# Revit family: Rohrschelle Maxima PSM, M 8-M10, Ø 15- 64, Gummi
name_source: partatom
category: HLS-Bauteile
revit_build: Autodesk Revit 2017 (Build: 20190507_1515(x64)
units: mm (PartAtom-declared; Revit-internal decimal feet)

## family parameters
Arbeitsebenenbasiert = Nein
Beim Laden mit Abzugskörper schneiden = Nein
Bemaßung runder Anschluss = Durchmesser verwenden
Gemeinsam genutzt = Ja
Immer vertikal = Nein
Raumberechnungspunkt = Nein
Teiletyp = Normal

## types (8) — shared parameters
A = 31 mm  [stored 0.101706 ft]
Anschluss = M8/M10
Anschlußhöhe = 30 mm
Bauart = zweiteilig
Baustoffklasse = B2
Brandschutz = RAL-GZ 656
DF1 = 24 mm  [stored 0.0787402 ft]
DF2 = 20 mm  [stored 0.0656168 ft]
DS = 6 mm  [stored 0.019685 ft]
DVS = 15 mm  [stored 0.0492126 ft]
Dämmstärke = 6 mm  [stored 0.019685 ft]
Fabrikat = MEFA
Farbe Schalldämmeinlage = schwarz
Firma = MEFA Befestigungs- und Montagesysteme GmbH
HGA = 22 mm  [stored 0.0721785 ft]
Kurztext1 = Rohrschelle Maxima PSM 25x3,0
MB = 25 mm  [stored 0.082021 ft]
MD = 3 mm  [stored 0.00984252 ft]
Material = Stahl
Material Schalldämmeinlage = TPE
Materialmaße = 25x3,0 mm
Materialname = S235
Mengeneinheit = St
Oberflaeche = galvanisch verzinkt
Schalldämmeinlage = Gummi
Verschluss = Pendelsteckmuttern
Verschluss-Schraube = M8
max. Temperaturbeständigkeit = 100 °C
max. zul. Last = 1.50 kN
max. zul. Last horizontal = 0.00 kN
max. zul. Last vertikal = 0.00 kN
vpe = 1 St
zero-valued in all types: Nennweite DN Rohr, Rohraußendurchmesser, Stärke Material

## per-type parameters (varying)
| type | AB | Achsabstand | Artikelnummer | B | Breite | D | D0 | Dmax | Dmin | EAN | Gewicht | Gewicht pro Bauteil | H | Kurztext2 | R | RM | Rohraußendurchmesser Zoll | S | max. Höhe | max. Rohraußendurchmesser | min. Rohraußendurchmesser |
| Maxima PSM, M8/M10, Ø 15- 19, Gummi | 4 mm  [stored 0.0131234 ft] | 57 mm | 0068819 | 81 mm | 81 mm | 19 mm  [stored 0.062336 ft] | 31 mm  [stored 0.101706 ft] | 19 mm  [stored 0.062336 ft] | 15 mm  [stored 0.0492126 ft] | 4250928402363 | 0.20 kg | 0.20 kg | 59 mm  [stored 0.19357 ft] | 15 - 19 mm M8/M10 TPE | 16 mm  [stored 0.0524934 ft] | 19 mm  [stored 0.062336 ft] | Zoll | 57 mm  [stored 0.187008 ft] | 58 mm  [stored 0.190289 ft] | 19 mm  [stored 0.062336 ft] | 15 mm  [stored 0.0492126 ft] |
| Maxima PSM, M8/M10, Ø 20- 25, Gummi | 5 mm  [stored 0.0164042 ft] | 63 mm | 0068823 | 87 mm | 87 mm | 25 mm  [stored 0.082021 ft] | 37 mm  [stored 0.121391 ft] | 25 mm  [stored 0.082021 ft] | 20 mm  [stored 0.0656168 ft] | 4250928402370 | 0.21 kg | 0.21 kg | 65 mm  [stored 0.213255 ft] | 20 - 25 mm M8/M10 TPE | 19 mm  [stored 0.062336 ft] | 22 mm  [stored 0.0721785 ft] | 1/2 Zoll | 63 mm | 64 mm  [stored 0.209974 ft] | 25 mm  [stored 0.082021 ft] | 20 mm  [stored 0.0656168 ft] |
| Maxima PSM, M8/M10, Ø 26- 30, Gummi | 4 mm  [stored 0.0131234 ft] | 68 mm | 0068828 | 92 mm | 92 mm | 30 mm  [stored 0.0984252 ft] | 42 mm | 30 mm  [stored 0.0984252 ft] | 26 mm | 4250928402387 | 0.22 kg | 0.22 kg | 70 mm | 26 - 30 mm M8/M10 TPE | 21 mm  [stored 0.0688976 ft] | 24 mm  [stored 0.0787402 ft] | 3/4 Zoll | 68 mm | 69 mm  [stored 0.226378 ft] | 30 mm  [stored 0.0984252 ft] | 26 mm |
| Maxima PSM, M8/M10, Ø 31- 36, Gummi | 5 mm  [stored 0.0164042 ft] | 74 mm | 0068873 | 98 mm | 98 mm | 36 mm  [stored 0.11811 ft] | 48 mm  [stored 0.15748 ft] | 36 mm  [stored 0.11811 ft] | 31 mm  [stored 0.101706 ft] | 4250928402516 | 0.23 kg | 0.23 kg | 76 mm | 31 - 36 mm M8/M10 TPE | 24 mm  [stored 0.0787402 ft] | 27 mm  [stored 0.0885827 ft] | 1 Zoll | 74 mm | 75 mm | 36 mm  [stored 0.11811 ft] | 31 mm  [stored 0.101706 ft] |
| Maxima PSM, M8/M10, Ø 38- 45, Gummi | 7 mm  [stored 0.0229659 ft] | 83 mm | 0068880 | 107 mm | 107 mm | 45 mm  [stored 0.147638 ft] | 57 mm  [stored 0.187008 ft] | 45 mm  [stored 0.147638 ft] | 38 mm  [stored 0.124672 ft] | 4250928402547 | 0.25 kg | 0.25 kg | 85 mm | 38 - 45 mm M8/M10 TPE | 29 mm | 32 mm  [stored 0.104987 ft] | 1 1/4 Zoll | 83 mm | 84 mm | 45 mm  [stored 0.147638 ft] | 38 mm  [stored 0.124672 ft] |
| Maxima PSM, M8/M10, Ø 47- 51, Gummi | 4 mm  [stored 0.0131234 ft] | 89 mm | 0068881 | 113 mm | 113 mm | 51 mm | 63 mm | 51 mm | 47 mm  [stored 0.154199 ft] | 4250928402554 | 0.27 kg | 0.27 kg | 91 mm | 47 - 51 mm M8/M10 TPE | 32 mm  [stored 0.104987 ft] | 35 mm  [stored 0.114829 ft] | 1 1/2 Zoll | 89 mm | 90 mm | 51 mm | 47 mm  [stored 0.154199 ft] |
| Maxima PSM, M8/M10, Ø 53- 57, Gummi | 4 mm  [stored 0.0131234 ft] | 95 mm | 0068941 | 119 mm | 119 mm | 57 mm  [stored 0.187008 ft] | 69 mm  [stored 0.226378 ft] | 57 mm  [stored 0.187008 ft] | 53 mm  [stored 0.173885 ft] | 4250928402677 | 0.29 kg | 0.29 kg | 97 mm | 53 - 57 mm M8/M10 TPE | 35 mm  [stored 0.114829 ft] | 38 mm  [stored 0.124672 ft] | Zoll | 95 mm | 96 mm | 57 mm  [stored 0.187008 ft] | 53 mm  [stored 0.173885 ft] |
| Maxima PSM, M8/M10, Ø 58- 64, Gummi | 6 mm  [stored 0.019685 ft] | 102 mm | 00688083 | 126 mm | 126 mm | 64 mm  [stored 0.209974 ft] | 76 mm | 64 mm  [stored 0.209974 ft] | 58 mm  [stored 0.190289 ft] | 4250928402356 | 0.30 kg | 0.30 kg | 104 mm | 58 - 64 mm M8/M10 TPE | 38 mm  [stored 0.124672 ft] | 41 mm  [stored 0.134514 ft] | 2 Zoll | 102 mm | 103 mm | 64 mm  [stored 0.209974 ft] | 58 mm  [stored 0.190289 ft] |

note: [stored X ft] marks values corroborated as IEEE doubles in the binary element streams (Revit-internal decimal feet)

## geometry (parser evidence)
native form markers: Sweep x6
no freeform markers — native parametric forms only
